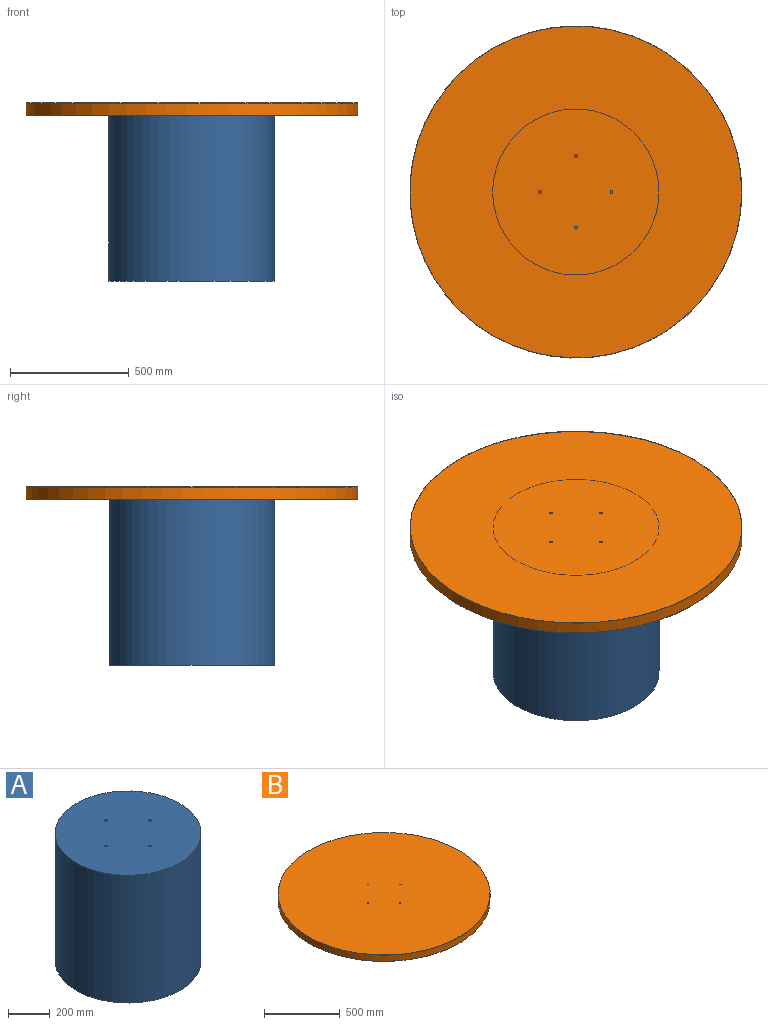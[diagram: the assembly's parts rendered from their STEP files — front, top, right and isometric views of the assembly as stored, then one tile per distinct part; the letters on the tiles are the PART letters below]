
ASSEMBLY  parts=2 mates=1
PART A: 11 faces, bbox 700x700x750 mm
  f0: cylinder r=350mm len=750mm, axis (0,0,-1), area 1649336.1mm2, adj f1,f2
  f1: plane 700x700mm, normal (0,0,1), area 384392.7mm2, adj f0,f3,f5,f7,f9
  f2: plane 700x700mm, normal (0,0,-1), area 384845.1mm2, adj f0
  f3: cylinder r=6mm len=300mm, axis (0,0,1), area 11309.7mm2, adj f1,f4
  f4: plane 12x12mm, normal (0,0,1), area 113.1mm2, adj f3
  f5: cylinder r=6mm len=300mm, axis (0,0,1), area 11309.7mm2, adj f1,f6
  f6: plane 12x12mm, normal (0,0,1), area 113.1mm2, adj f5
  f7: cylinder r=6mm len=300mm, axis (0,0,1), area 11309.7mm2, adj f1,f8
  f8: plane 12x12mm, normal (0,0,1), area 113.1mm2, adj f7
  f9: cylinder r=6mm len=300mm, axis (0,0,1), area 11309.7mm2, adj f1,f10
  f10: plane 12x12mm, normal (0,0,1), area 113.1mm2, adj f9
PART B: 13 faces, bbox 1400x1400x302 mm
  f0: cylinder r=700mm len=1400mm, axis (0,0,-1), area 228707.9mm2, adj f1,f3
  f1: plane 1400x1400mm, normal (0,0,1), area 1539380.4mm2, adj f0
  f2: cylinder r=699mm len=1398mm, axis (0,0,1), area 219597.3mm2, adj f3,f4
  f3: plane 1400x1400mm, normal (0,0,-1), area 4395.1mm2, adj f0,f2
  f4: plane 1398x1398mm, normal (0,0,-1), area 1534532.9mm2, adj f2,f5,f7,f9,f11
  f5: cylinder r=6mm len=300mm, axis (0,0,1), area 11309.7mm2, adj f4,f6
  f6: plane 12x12mm, normal (0,0,-1), area 113.1mm2, adj f5
  f7: cylinder r=6mm len=300mm, axis (0,0,1), area 11309.7mm2, adj f4,f8
  f8: plane 12x12mm, normal (0,0,-1), area 113.1mm2, adj f7
  f9: cylinder r=6mm len=300mm, axis (0,0,1), area 11309.7mm2, adj f4,f10
  f10: plane 12x12mm, normal (0,0,-1), area 113.1mm2, adj f9
  f11: cylinder r=6mm len=300mm, axis (0,0,1), area 11309.7mm2, adj f4,f12
  f12: plane 12x12mm, normal (0,0,-1), area 113.1mm2, adj f11
PLACE A t=(0,0,-750)mm
PLACE B at identity
MATE cylindrical A.f7 <-> B.f5  axis (0,0,1) through (0,-150,0)mm
